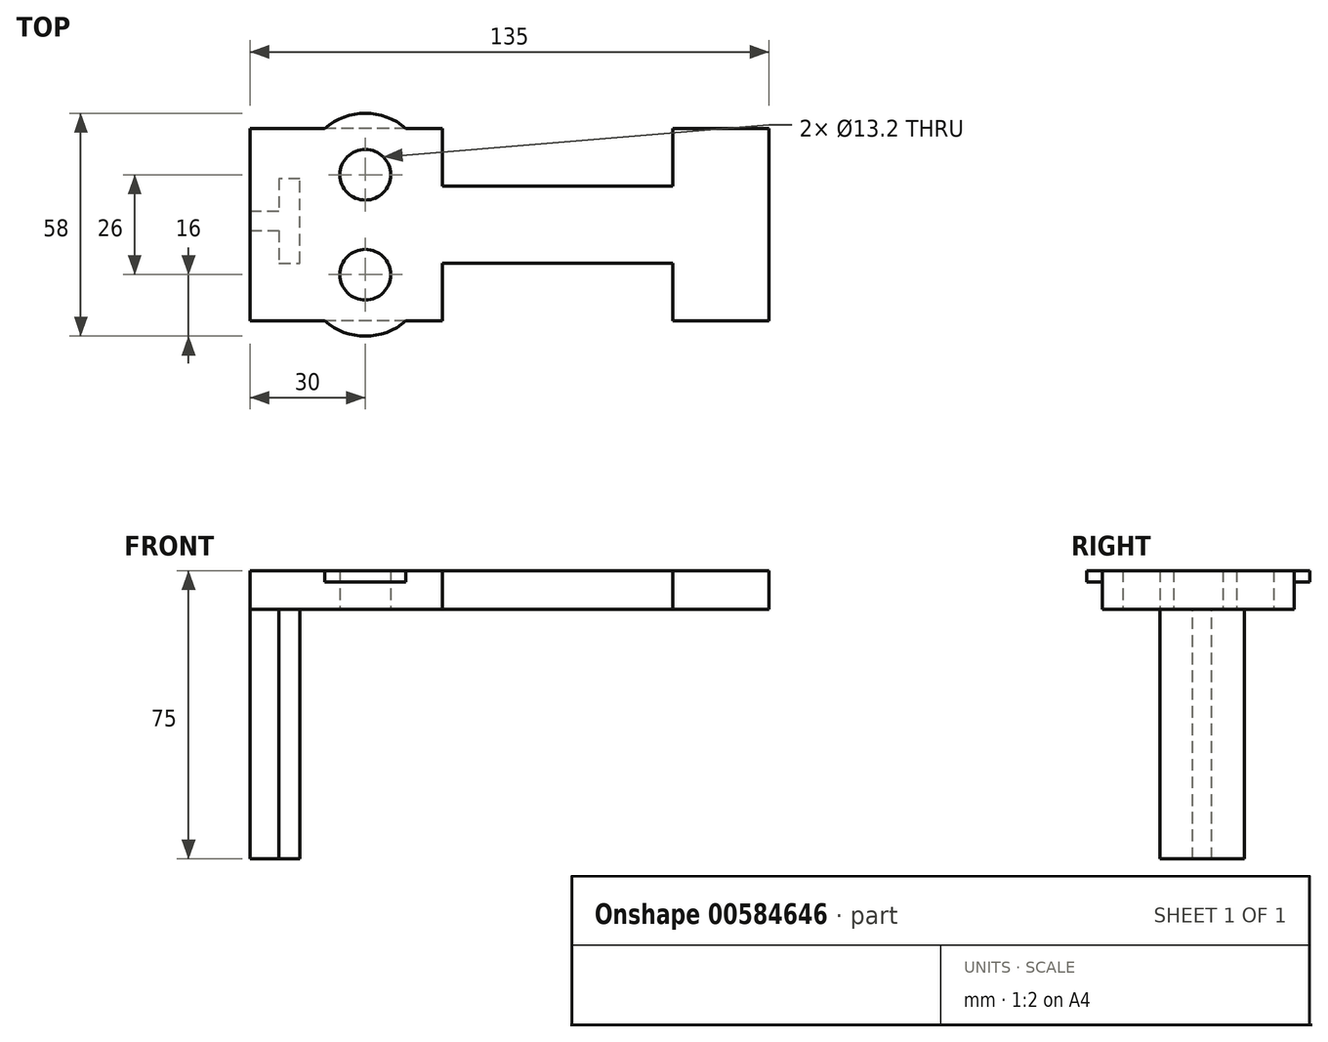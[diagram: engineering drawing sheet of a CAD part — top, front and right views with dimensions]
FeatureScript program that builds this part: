
annotation { "Feature Type Name" : "Feature", "Feature Type Description" : "" }
export const myFeature = defineFeature(function(context is Context, id is Id, definition is map)
    precondition{}
    {
        {
            var Q0;
            Q0=qCreatedBy(makeId("Front.planeOp"),FACE);
            var sketch = newSketch(context, id + "F0", { "sketchPlane" : qUnion([Q0])});
            skLineSegment(sketch, "E0.bottom", {"start": v(67.5, 5) * mm, "end": v(-67.5, 5) * mm});
            skLineSegment(sketch, "E0.top", {"start": v(67.5, -5) * mm, "end": v(-67.5, -5) * mm});
            skLineSegment(sketch, "E0.left", {"start": v(67.5, 5) * mm, "end": v(67.5, -5) * mm});
            skLineSegment(sketch, "E0.right", {"start": v(-67.5, 5) * mm, "end": v(-67.5, -5) * mm});
            skPoint(sketch, "E0.middle", {"position": v(0, 0) * mm});
            skSolve(sketch);
        }
        {
            var Q0;
            Q0=makeQuery(id+"F0.imprint","IMPRINT",FACE,{"disambiguationData":[TD([[makeQuery(id+"F0.imprint","IMPRINT",EDGE,{"derivedFrom":sQuery(id+"F0.wireOp",EDGE,"E0.top")}),-1.0]])]});
            extrude(context, id + "F1", {"entities" : qUnion([Q0]), "endBound" : BoundingType.SYMMETRIC, "depth" : 50 * mm, "offsetDistance" : 25 * mm});
        }
        {
            var Q0;
            Q0=makeQuery(id+"F1.opExtrude","SWEPT_FACE",FACE,{"disambiguationData":[OSD([sQuery(id+"F0.wireOp",EDGE,"E0.top")])]});
            var sketch = newSketch(context, id + "F2", { "sketchPlane" : qUnion([Q0])});
            skPoint(sketch, "E1", {"position": v(-37.5, 13) * mm});
            skPoint(sketch, "E2", {"position": v(-37.5, -13) * mm});
            skSolve(sketch);
        }
        {
            var Q0;
            Q0=makeQuery(id+"F1.opExtrude","SWEPT_FACE",FACE,{"disambiguationData":[OSD([sQuery(id+"F0.wireOp",EDGE,"E0.bottom")])]});
            var sketch = newSketch(context, id + "F3", { "sketchPlane" : qUnion([Q0])});
            skLineSegment(sketch, "E3", {"start": v(-67.5, 3.5) * mm, "end": v(-60, 3.5) * mm});
            skLineSegment(sketch, "E4", {"start": v(-60, 3.5) * mm, "end": v(-60, 12) * mm});
            skLineSegment(sketch, "E5", {"start": v(-60, 12) * mm, "end": v(-54.5, 12) * mm});
            skLineSegment(sketch, "E6", {"start": v(-54.5, 12) * mm, "end": v(-54.5, -10) * mm});
            skLineSegment(sketch, "E7", {"start": v(-54.5, -10) * mm, "end": v(-60, -10) * mm});
            skLineSegment(sketch, "E8", {"start": v(-60, -10) * mm, "end": v(-60, -1.5) * mm});
            skLineSegment(sketch, "E9", {"start": v(-60, -1.5) * mm, "end": v(-67.5, -1.5) * mm});
            skLineSegment(sketch, "E10", {"start": v(-67.5, -1.5) * mm, "end": v(-67.5, 3.5) * mm});
            skSolve(sketch);
        }
        {
            var Q0;
            Q0=qSketchRegion(id+"F3",true);
            extrude(context, id + "F4", {"entities" : qUnion([Q0]), "operationType" : NewBodyOperationType.ADD, "oppositeDirection" : true, "depth" : 75 * mm, "offsetDistance" : 25 * mm});
        }
        {
            var Q0;
            Q0=makeQuery(id+"F1.opExtrude","SWEPT_FACE",FACE,{"disambiguationData":[OSD([sQuery(id+"F0.wireOp",EDGE,"E0.bottom")])]});
            var sketch = newSketch(context, id + "F5", { "sketchPlane" : qUnion([Q0])});
            skCircle(sketch, "E11", {"center": v(-37.5, 13) * mm, "radius": 16 * mm});
            skCircle(sketch, "E12", {"center": v(-37.5, -13) * mm, "radius": 16 * mm});
            skSolve(sketch);
        }
        {
            var Q0;
            Q0 = qSketchRegion(id + "F5", true);
            extrude(context, id + "F6", {"entities" : qUnion([Q0]), "operationType" : NewBodyOperationType.ADD, "oppositeDirection" : true, "depth" : 3 * mm, "offsetDistance" : 25 * mm});
        }
        {
            var Q0;
            Q0=makeQuery(id+"F1.opExtrude","SWEPT_FACE",FACE,{"disambiguationData":[OSD([sQuery(id+"F0.wireOp",EDGE,"E0.top")])]});
            var sketch = newSketch(context, id + "F7", { "sketchPlane" : qUnion([Q0])});
            skLineSegment(sketch, "E13.bottom", {"start": v(-17.5, 25) * mm, "end": v(42.5, 25) * mm});
            skLineSegment(sketch, "E13.top", {"start": v(-17.5, 10) * mm, "end": v(42.5, 10) * mm});
            skLineSegment(sketch, "E13.left", {"start": v(-17.5, 25) * mm, "end": v(-17.5, 10) * mm});
            skLineSegment(sketch, "E13.right", {"start": v(42.5, 25) * mm, "end": v(42.5, 10) * mm});
            skLineSegment(sketch, "E14.bottom", {"start": v(-17.5, -25) * mm, "end": v(42.5, -25) * mm});
            skLineSegment(sketch, "E14.top", {"start": v(-17.5, -10) * mm, "end": v(42.5, -10) * mm});
            skLineSegment(sketch, "E14.left", {"start": v(-17.5, -25) * mm, "end": v(-17.5, -10) * mm});
            skLineSegment(sketch, "E14.right", {"start": v(42.5, -25) * mm, "end": v(42.5, -10) * mm});
            skSolve(sketch);
        }
        {
            var Q0;
            Q0 = qSketchRegion(id + "F7", true);
            extrude(context, id + "F8", {"entities" : qUnion([Q0]), "operationType" : NewBodyOperationType.REMOVE, "oppositeDirection" : true, "depth" : 25 * mm, "offsetDistance" : 25 * mm});
        }
        {
            var Q0;
            Q0=sQuery(id+"F2.wireOp",VERTEX,"E1");
            var Q1;
            Q1=sQuery(id+"F2.wireOp",VERTEX,"E2");
            var Q2;
            Q2=makeQuery(id+"F1.opExtrude","SWEPT_BODY",BODY,{"disambiguationData":[OSD([sQuery(id+"F0.wireOp",EDGE,"E0.bottom"),sQuery(id+"F0.wireOp",EDGE,"E0.top"),sQuery(id+"F0.wireOp",EDGE,"E0.left"),sQuery(id+"F0.wireOp",EDGE,"E0.right")])]});
            hole(context, id + "F9", {"style" : HoleStyle.C_BORE, "endStyle" : HoleEndStyle.THROUGH, "holeDiameter" : 13.2 * mm, "cBoreDiameter" : 23 * mm, "cBoreDepth" : 0 * mm, "majorDiameter" : 5 * mm, "isTappedThrough" : true, "tappedDepth" : 12 * mm, "tapClearance" : 3, "startFromSketch" : true, "locations" : qUnion([Q0, Q1]), "scope" : qUnion([Q2])});
        }
    });
